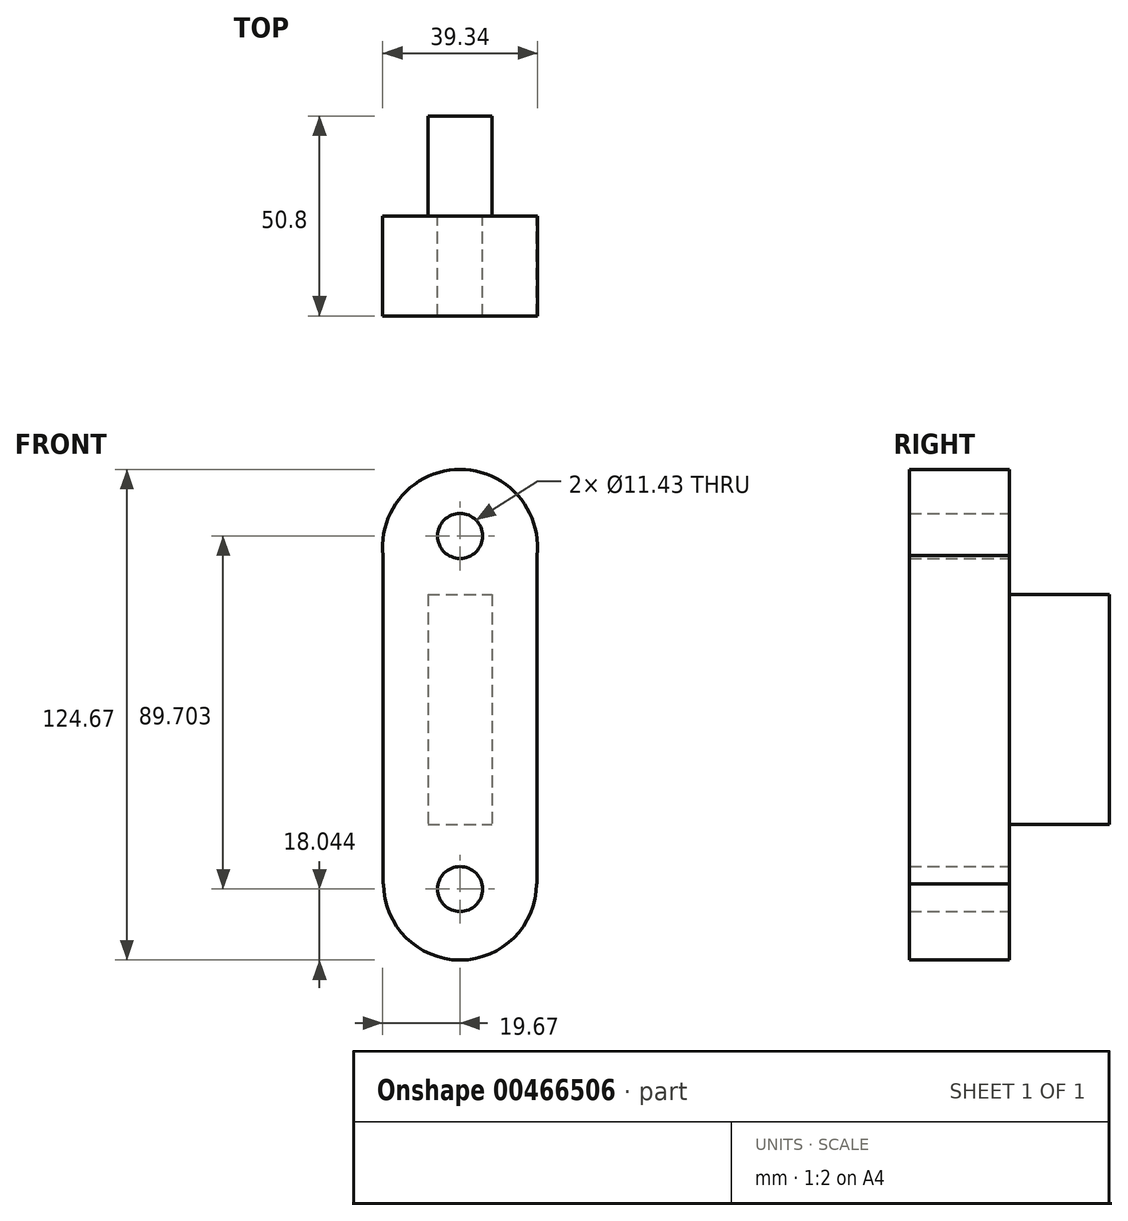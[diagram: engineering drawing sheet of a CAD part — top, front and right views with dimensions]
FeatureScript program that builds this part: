
annotation { "Feature Type Name" : "Feature", "Feature Type Description" : "" }
export const myFeature = defineFeature(function(context is Context, id is Id, definition is map)
    precondition{}
    {
        {
            var Q0;
            Q0=qCreatedBy(makeId("Front.planeOp"),FACE);
            var sketch = newSketch(context, id + "F0", { "sketchPlane" : qUnion([Q0])});
            skLineSegment(sketch, "E0.bottom", {"start": v(-19.55, 42.8) * mm, "end": v(19.55, 42.8) * mm});
            skLineSegment(sketch, "E0.top", {"start": v(-19.55, -42.8) * mm, "end": v(19.55, -42.8) * mm});
            skLineSegment(sketch, "E0.left", {"start": v(-19.55, 42.8) * mm, "end": v(-19.55, -42.8) * mm});
            skLineSegment(sketch, "E0.right", {"start": v(19.55, 42.8) * mm, "end": v(19.55, -42.8) * mm});
            skPoint(sketch, "E0.middle", {"position": v(0, 0) * mm});
            skCircle(sketch, "E1", {"center": v(0, 42.8) * mm, "radius": 19.67 * mm});
            skCircle(sketch, "E2", {"center": v(0, -42.8) * mm, "radius": 19.4 * mm});
            skSolve(sketch);
        }
        {
            var Q0;
            Q0 = qSketchRegion(id + "F0", true);
            extrude(context, id + "F1", {"entities" : qUnion([Q0]), "depth" : 25.4 * mm});
        }
        {
            var Q0;
            Q0=qCreatedBy(makeId("Front.planeOp"),FACE);
            var sketch = newSketch(context, id + "F2", { "sketchPlane" : qUnion([Q0])});
            skCircle(sketch, "E3", {"center": v(0, 45.55) * mm, "radius": 5.72 * mm});
            skCircle(sketch, "E4", {"center": v(0, -44.16) * mm, "radius": 5.72 * mm});
            skSolve(sketch);
        }
        {
            var Q0;
            Q0 = qSketchRegion(id + "F2", true);
            extrude(context, id + "F3", {"entities" : qUnion([Q0]), "operationType" : NewBodyOperationType.REMOVE, "depth" : 25.4 * mm});
        }
        {
            var Q0;
            Q0=qCreatedBy(makeId("Front.planeOp"),FACE);
            var sketch = newSketch(context, id + "F4", { "sketchPlane" : qUnion([Q0])});
            skLineSegment(sketch, "E5.bottom", {"start": v(-8.18, 30.7) * mm, "end": v(8.15, 30.7) * mm});
            skLineSegment(sketch, "E5.top", {"start": v(-8.18, -27.76) * mm, "end": v(8.15, -27.76) * mm});
            skLineSegment(sketch, "E5.left", {"start": v(-8.18, 30.7) * mm, "end": v(-8.18, -27.76) * mm});
            skLineSegment(sketch, "E5.right", {"start": v(8.15, 30.7) * mm, "end": v(8.15, -27.76) * mm});
            skSolve(sketch);
        }
        {
            var Q0;
            Q0 = qSketchRegion(id + "F4", true);
            extrude(context, id + "F5", {"entities" : qUnion([Q0]), "operationType" : NewBodyOperationType.ADD, "oppositeDirection" : true, "depth" : 25.4 * mm});
        }
    });
